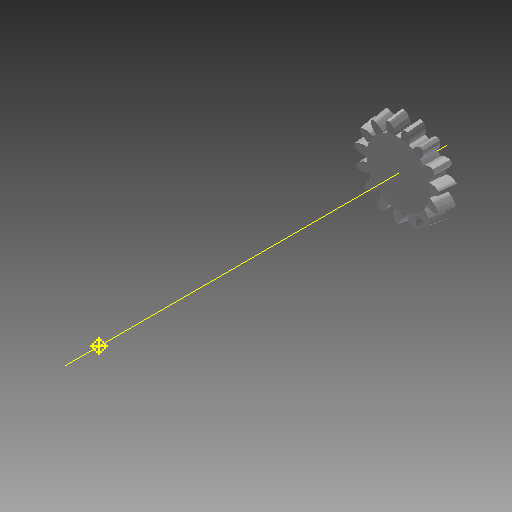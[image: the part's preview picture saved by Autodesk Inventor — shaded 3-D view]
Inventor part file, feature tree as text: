
AUTODESK INVENTOR PART (.ipt)
format: ipt  version: 2017 (Build 210142000, 142)  size: 500,736 bytes
history: native  units: mm
features: other x24, loft x2, pattern_circular x2, sketch x2
ambient origin geometry x6: Origin, XZ Plane, X Axis, Y Axis, Z Axis, Center Point
bodies: Solid1 (feature_tree)
feature tree (30):
  other  "Top Point"
  other  "Mesh Plane2"
  other  "Teeth Body"
  other  "Start Point"
  other  "Tooth Plane"
  other  "Start Sketch"
  other  "End Point"
  other  "3D Sketch Right"
  other  "End Plane Right"
  loft  "Loft Right"
  pattern_circular  "Circular Pattern Right"  [2 undecoded]
  other  "3D Sketch Left"
  other  "End Plane Left"
  loft  "Loft Left"
  pattern_circular  "Circular Pattern Left"  Angle=90.0deg  [1 undecoded]
  other  "Fix Body"
  sketch  "Sketch8"  dims[d2=42.950477mm d3=7.62mm d4=150.824298mm d5=90.0deg d7=7.258789mm d8=8.466511mm d9=15.816659mm d11=7.894621mm d12=6.889845mm d15=8.036182mm d16=15.012743mm d17=0.0mm d18=90.0deg d19=0.0mm d20=90.0deg d21=150.0mm d22=360.0deg d26=314.208686mm d27=7.832641mm d28=38.1mm d29=-1.253891mm d30=6.889845mm d31=8.036182mm d32=15.012743mm d35=0.0mm d37=0.0mm d39=0.0mm d40=90.0deg d41=150.0mm d42=360.0deg d46=90.0deg d47=90.0deg d48=0.0mm d49=0.0mm d50=90.0deg d51=2.094395mm d52=0.0mm d53=0.0mm d54=0.0mm d56=20.24081mm d57=23.292902mm d58=15.493652mm d59=22.10899mm d60=14.706153mm d61=22.10899mm d62=14.706153mm d63=90.0deg d64=90.0deg d65=314.208686mm d66=31.5mm d67=38.1mm d68=-1.253891mm d69=7.832641mm d70=8.036182mm d71=15.012743mm d72=6.889845mm d73=14.706153mm d74=22.10899mm d75=0.0mm d76=90.0deg d77=0.0mm d78=90.0deg d79=0.0mm d80=90.0deg d81=150.0mm d82=360.0deg d84=10.0mm d85=20.0mm d86=20.0mm d87=10.0mm d88=0.0mm d89=0.0mm]
  other  "Mesh Plane"
  other  "Top Plane"
  other  "Teeth Body Sketch"
  other  "End Plane"
  other  "End Sketch"
  other  "Helical Curve Left"
  other  "End Sketch Left"
  other  "Body Sketch"
  sketch  "Sketch6"  dims[d0=38.1mm d1=32.051859mm]
  other  "Srf1"
  other  "Helical Curve Right"
  other  "End Sketch Right"
  other  "Pitch Diameter"
note: 3 required parameter values undecoded (feature->parameter linkage not recoverable at this tier; creation-order binding heuristic only, values carry confidence <= 0.55)
